# Revit family: Shower-Handshower_Kit-KOHLER-Spatula-K-98445IN
name_source: partatom
category: Plumbing Fixtures
units: mm (PartAtom-declared; Revit-internal decimal feet)

## family parameters
Cut with Voids When Loaded = No
Host = Face
Maintain Annotation Orientation = No
OmniClass Number = 23.31.17.00
OmniClass Title = Showers
Part Type = Normal
Room Calculation Point = No
Round Connector Dimension = Use Diameter
Shared = No

## types (6) — shared parameters
ADA Compliant = No
Assembly Code = D2010700
CW Connection = No
Cold Water Inlet = Cold Water Inlet
Date Modified = 08/17/2024
Default Elevation = 3' - 6"
Description = Square Single-Function Handshower, 13.0 LPM
Drain Included = No
Flow Rate = 3 GPM
HW Connection = Yes
Height = 0' - 9 3/8"
Hose Included = Yes
Hot Water Inlet = Hot Water Inlet
Length = 0' - 4 3/16"
Manufacturer = Kohler Co.
Master Format 2014 = 22 42 23
Master Format 2014 Name = Residential Showers
Material = Plastic
Pressure = 188.00 psi
Product Name = Spatula
Tempered Water Inlet = Tempered Water Inlet
URL = https://www.kohler.co.in
Vent Connection = No
Waste Connection = No
Waste Water Outlet = Waste Water Outlet
WaterSense Certified = No
Width = 0' - 3 7/8"

## per-type parameters (varying)
| type | Finish | Model | Product Page URL | Type |
| CP-Polished Chrome | Kohler-Plastic-CP-Polished_Chrome | K-98445IN-CP | https://www.kohler.co.in | 1 |
| AF-Vibrant French Gold | KOHLER-Plastic-AF-Vibrant_French_Gold | K-98445IN-AF | https://www.kohler.co.in | 2 |
| BV-Brushed Bronze | Kohler-Plastic-BV-Brushed_Bronze | K-98445IN-BV | https://www.kohler.co.in | 3 |
| BN-Vibrant Brushed Nickel | KOHLER-Plastic-BN-Vibrant_Brushed_Nickel | K-98445IN-BN |  | 4 |
| BL-Matte Black | Kohler-Plastic-BL-Matte_Black | K-98445IN-BL | https://www.kohler.co.in | 5 |
| BRD-Brushed Rose Gold | Kohler-Plastic-BRD-Brushed_Rose_Gold | K-98445IN-BRD |  | 6 |

## geometry (parser evidence)
native form markers: Sweep x5
no freeform markers — native parametric forms only
